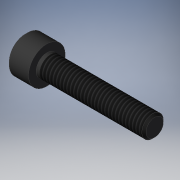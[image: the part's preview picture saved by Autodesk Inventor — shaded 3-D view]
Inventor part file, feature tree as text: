
AUTODESK INVENTOR PART (.ipt)
format: ipt  version: 2019 (Build 230136000, 136)  size: 150,016 bytes
history: native  units: mm
features: other x14, sketch x3, revolve x1, thread x1, hole x1, extrude x1
ambient origin geometry x8: Origin, YZ Plane, XZ Plane, XY Plane, X Axis, Y Axis, Z Axis, Center Point
bodies: Solid1 (feature_tree)
feature tree (21):
  revolve  "Revolution1"  [1 undecoded]
  thread  "Thread1"  [1 undecoded]
  hole  "Hole1"  [1 undecoded]
  extrude  "Extrusion1"  [1 undecoded]
  other  "bolt_XY"
  other  "bolt_YZ"
  other  "bolt_ZX"
  other  "bolt_X"
  other  "bolt_Y"
  other  "bolt_Z"
  other  "bolt_Center"
  other  "nut_XY"
  other  "nut_YZ"
  other  "nut_ZX"
  other  "nut_X"
  other  "nut_Y"
  other  "nut_Z"
  other  "nut_Center"
  sketch  "Sketch_1"  dims[d0=360.0deg d1=24.2mm d2=0.8mm]
  sketch  "Sketch2"  dims[d3=4.0mm d4=6.0mm d5=4.0mm d6=2.0mm d7=90.0deg d8=2.5mm d9=120.0deg d10=2.5mm d11=0.0mm]
  sketch  "Sketch_3"  dims[d12=0.0mm d13=0.0mm]
note: 4 required parameter values undecoded (feature->parameter linkage not recoverable at this tier; creation-order binding heuristic only, values carry confidence <= 0.55)